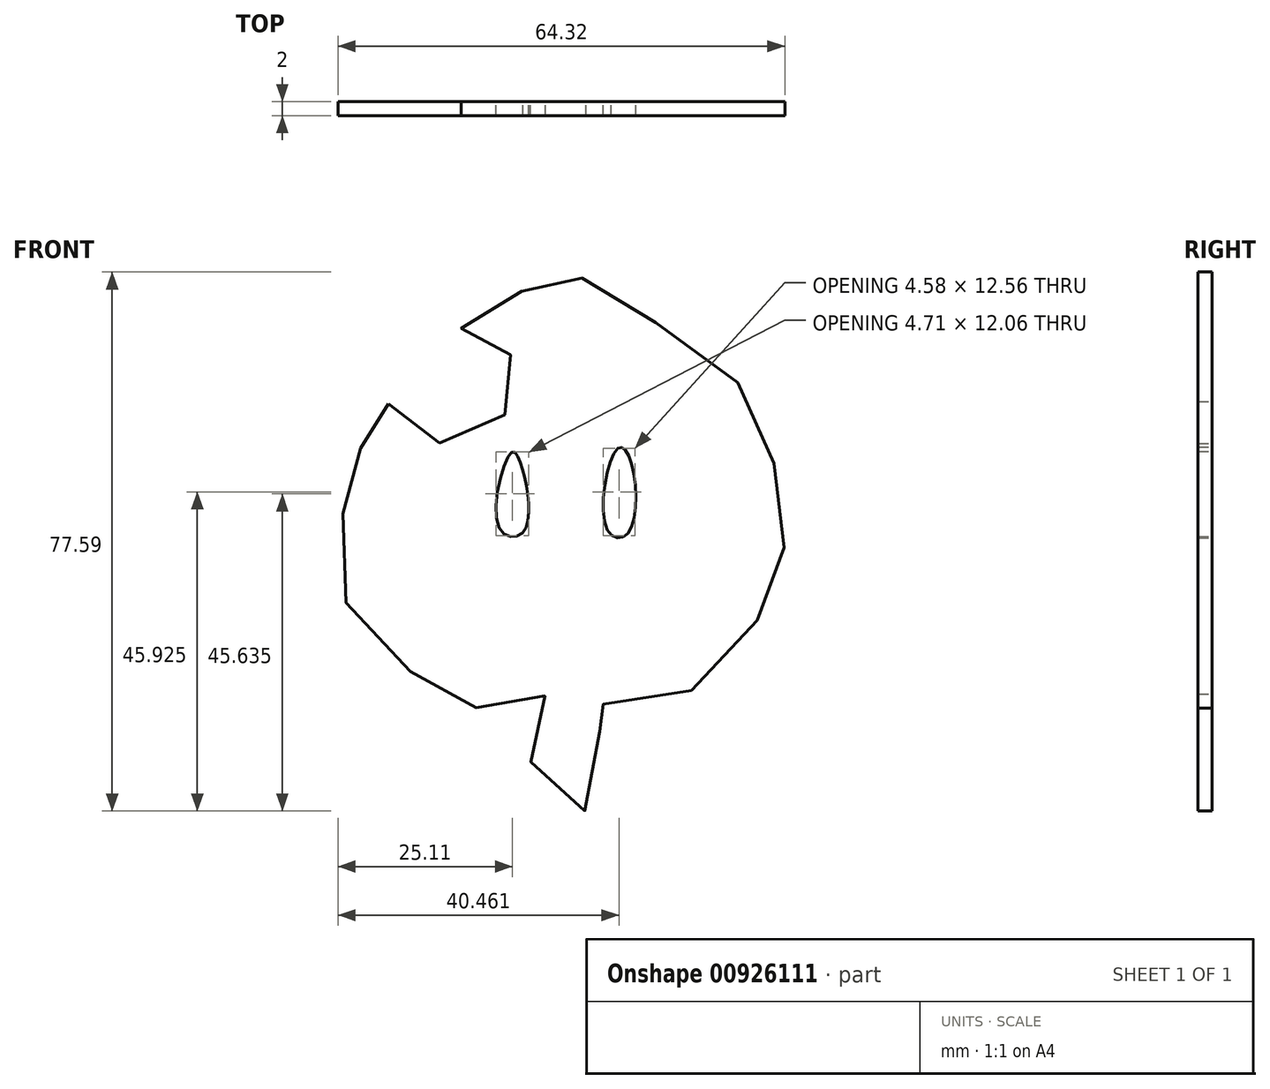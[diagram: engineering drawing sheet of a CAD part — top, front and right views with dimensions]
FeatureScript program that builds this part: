
annotation { "Feature Type Name" : "Feature", "Feature Type Description" : "" }
export const myFeature = defineFeature(function(context is Context, id is Id, definition is map)
    precondition{}
    {
        {
            var Q0;
            Q0=qCreatedBy(makeId("Front.planeOp"),FACE);
            var sketch = newSketch(context, id + "F0", { "sketchPlane" : qUnion([Q0])});
            skFitSpline(sketch, "E0", {"points": [v(-57.05, 56.52) * mm, v(-57.6, 56.79) * mm, v(-61.35, 49.27) * mm, v(-63.36, 42.02) * mm, v(-63.36, 28.33) * mm, v(-52.76, 17.05) * mm, v(-44.17, 12.75) * mm, v(-34.77, 14.63) * mm, v(-35.3, 10.87) * mm, v(-35.04, 0) * mm, v(-25.37, 0) * mm, v(-28.6, 14.63) * mm, v(-26.18, 13.3) * mm, v(-12.22, 15.98) * mm, v(-2.55, 28.06) * mm, v(0, 37.73) * mm, v(-2.55, 51.15) * mm, v(-10.07, 62.96) * mm, v(-26.18, 72.36) * mm, v(-31.68, 75.46) * mm, v(-41.48, 70.48) * mm, v(-46.58, 67.26) * mm, v(-42.02, 65.38) * mm, v(-37.72, 59.47) * mm, v(-43.9, 52.22) * mm, v(-51.42, 51.42) * mm, v(-57.05, 56.52) * mm]});
            skSolve(sketch);
        }
        {
            var Q0;
            Q0=makeQuery(id+"F0.imprint","IMPRINT",FACE,{"disambiguationData":[TD([[makeQuery(id+"F0.imprint","IMPRINT",EDGE,{"derivedFrom":sQuery(id+"F0.wireOp",EDGE,"E0")}),1.0]])]});
            extrude(context, id + "F1", {"entities" : qUnion([Q0]), "depth" : 2 * mm, "offsetDistance" : 25.4 * mm});
        }
        {
            var Q0;
            Q0=makeQuery(id+"F1.opExtrude","CAP_FACE",FACE,{"disambiguationData":[OSD([sQuery(id+"F0.wireOp",EDGE,"E0")])],"isStart":false});
            var sketch = newSketch(context, id + "F2", { "sketchPlane" : qUnion([Q0])});
            skFitSpline(sketch, "E1", {"points": [v(-39.33, 49.54) * mm, v(-38.26, 48.46) * mm, v(-36.92, 42.56) * mm, v(-38, 37.72) * mm, v(-41.21, 38.8) * mm, v(-39.33, 49.54) * mm]});
            skFitSpline(sketch, "E2", {"points": [v(-24.03, 50.07) * mm, v(-22.15, 48.2) * mm, v(-22.69, 37.72) * mm, v(-25.64, 38.53) * mm, v(-24.03, 50.07) * mm]});
            skSolve(sketch);
        }
        {
            var Q0;
            Q0=makeQuery(id+"F2.imprint","IMPRINT",FACE,{"disambiguationData":[TD([[makeQuery(id+"F2.imprint","IMPRINT",EDGE,{"derivedFrom":sQuery(id+"F2.wireOp",EDGE,"E1")}),-1.0]])]});
            var Q1;
            Q1=makeQuery(id+"F2.imprint","IMPRINT",FACE,{"disambiguationData":[TD([[makeQuery(id+"F2.imprint","IMPRINT",EDGE,{"derivedFrom":sQuery(id+"F2.wireOp",EDGE,"E2")}),-1.0]])]});
            extrude(context, id + "F3", {"entities" : qUnion([Q0, Q1]), "operationType" : NewBodyOperationType.REMOVE, "oppositeDirection" : true, "depth" : 25 * mm, "offsetDistance" : 25 * mm});
        }
    });
